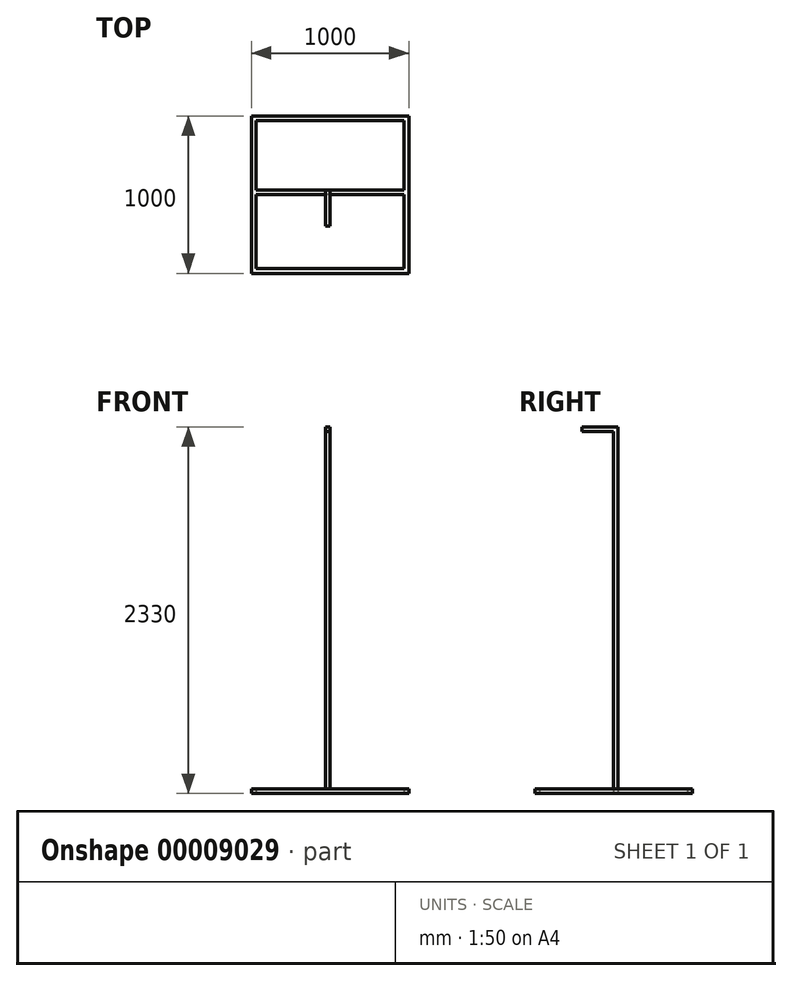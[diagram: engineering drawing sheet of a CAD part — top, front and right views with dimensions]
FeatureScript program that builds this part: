
annotation { "Feature Type Name" : "Feature", "Feature Type Description" : "" }
export const myFeature = defineFeature(function(context is Context, id is Id, definition is map)
    precondition{}
    {
        {
            var Q0;
            Q0=qCreatedBy(makeId("Top.planeOp"),FACE);
            var sketch = newSketch(context, id + "F0", { "sketchPlane" : qUnion([Q0])});
            skLineSegment(sketch, "E0.bottom", {"start": v(0, 0) * mm, "end": v(-1000, 0) * mm});
            skLineSegment(sketch, "E0.top", {"start": v(0, 1000) * mm, "end": v(-1000, 1000) * mm});
            skLineSegment(sketch, "E0.left", {"start": v(0, 0) * mm, "end": v(0, 1000) * mm});
            skLineSegment(sketch, "E0.right", {"start": v(-1000, 0) * mm, "end": v(-1000, 1000) * mm});
            skLineSegment(sketch, "E1.0", {"start": v(-30, 970) * mm, "end": v(-970, 970) * mm});
            skLineSegment(sketch, "E1.1", {"start": v(-30, 30) * mm, "end": v(-30, 970) * mm});
            skLineSegment(sketch, "E1.2", {"start": v(-30, 30) * mm, "end": v(-970, 30) * mm});
            skLineSegment(sketch, "E1.3", {"start": v(-970, 30) * mm, "end": v(-970, 970) * mm});
            skLineSegment(sketch, "E2.bottom", {"start": v(-970, 530) * mm, "end": v(-30, 530) * mm});
            skLineSegment(sketch, "E2.top", {"start": v(-970, 500) * mm, "end": v(-30, 500) * mm});
            skLineSegment(sketch, "E2.left", {"start": v(-970, 530) * mm, "end": v(-970, 500) * mm});
            skLineSegment(sketch, "E2.right", {"start": v(-30, 530) * mm, "end": v(-30, 500) * mm});
            skSolve(sketch);
        }
        {
            var Q0;
            Q0=makeQuery(id+"F0.imprint","IMPRINT",FACE,{"disambiguationData":[TD([[makeQuery(id+"F0.imprint","IMPRINT",EDGE,{"derivedFrom":sQuery(id+"F0.wireOp",EDGE,"E0.bottom")}),-1.0]])]});
            var Q1;
            Q1=makeQuery(id+"F0.imprint","IMPRINT",FACE,{"disambiguationData":[TD([[makeQuery(id+"F0.imprint","IMPRINT",EDGE,{"derivedFrom":sQuery(id+"F0.wireOp",EDGE,"E2.bottom")}),-1.0]])]});
            extrude(context, id + "F1", {"entities" : qUnion([Q0, Q1]), "depth" : 30 * mm});
        }
        {
            var Q0;
            Q0=makeQuery(id+"F1.opExtrude","CAP_FACE",FACE,{"disambiguationData":[OSD([sQuery(id+"F0.wireOp",EDGE,"E0.bottom"),sQuery(id+"F0.wireOp",EDGE,"E0.top"),sQuery(id+"F0.wireOp",EDGE,"E0.left"),sQuery(id+"F0.wireOp",EDGE,"E0.right"),sQuery(id+"F0.wireOp",EDGE,"E1.0"),sQuery(id+"F0.wireOp",EDGE,"E1.1"),sQuery(id+"F0.wireOp",EDGE,"E1.2"),sQuery(id+"F0.wireOp",EDGE,"E1.3"),sQuery(id+"F0.wireOp",EDGE,"E2.bottom"),sQuery(id+"F0.wireOp",EDGE,"E2.top")])],"isStart":false});
            var sketch = newSketch(context, id + "F2", { "sketchPlane" : qUnion([Q0])});
            skLineSegment(sketch, "E3.bottom", {"start": v(-500, 530) * mm, "end": v(-530, 530) * mm});
            skLineSegment(sketch, "E3.top", {"start": v(-500, 500) * mm, "end": v(-530, 500) * mm});
            skLineSegment(sketch, "E3.left", {"start": v(-500, 530) * mm, "end": v(-500, 500) * mm});
            skLineSegment(sketch, "E3.right", {"start": v(-530, 530) * mm, "end": v(-530, 500) * mm});
            skSolve(sketch);
        }
        {
            var Q0;
            Q0=makeQuery(id+"F2.imprint","IMPRINT",FACE,{"disambiguationData":[TD([[makeQuery(id+"F2.imprint","IMPRINT",EDGE,{"derivedFrom":sQuery(id+"F2.wireOp",EDGE,"E3.bottom")}),-1.0]])]});
            extrude(context, id + "F3", {"entities" : qUnion([Q0]), "operationType" : NewBodyOperationType.ADD, "depth" : 2300 * mm});
        }
        {
            var Q0;
            Q0=makeQuery(id+"F3.boolean.opBoolean","MERGE",FACE,{"derivedFrom":[makeQuery(id+"F1.opExtrude","SWEPT_FACE",FACE,{"disambiguationData":[OSD([sQuery(id+"F0.wireOp",EDGE,"E2.top")])]}),makeQuery(id+"F3.opExtrude","SWEPT_FACE",FACE,{"disambiguationData":[OSD([sQuery(id+"F2.wireOp",EDGE,"E3.top")])]})]});
            var sketch = newSketch(context, id + "F4", { "sketchPlane" : qUnion([Q0])});
            skLineSegment(sketch, "E4.bottom", {"start": v(-500, 2330) * mm, "end": v(-530, 2330) * mm});
            skLineSegment(sketch, "E4.top", {"start": v(-500, 2300) * mm, "end": v(-530, 2300) * mm});
            skLineSegment(sketch, "E4.left", {"start": v(-500, 2330) * mm, "end": v(-500, 2300) * mm});
            skLineSegment(sketch, "E4.right", {"start": v(-530, 2330) * mm, "end": v(-530, 2300) * mm});
            skSolve(sketch);
        }
        {
            var Q0;
            Q0=makeQuery(id+"F4.imprint","IMPRINT",FACE,{"disambiguationData":[TD([[makeQuery(id+"F4.imprint","IMPRINT",EDGE,{"derivedFrom":sQuery(id+"F4.wireOp",EDGE,"E4.bottom")}),-1.0]])]});
            extrude(context, id + "F5", {"entities" : qUnion([Q0]), "operationType" : NewBodyOperationType.ADD, "depth" : 200 * mm});
        }
    });
